# Revit family: Loudspeaker-Bollard-Q-SYS-AD-DWL-Subwoofer
name_source: partatom
category: Communication Devices
units: mm (PartAtom-declared; Revit-internal decimal feet)

## family parameters
Always vertical = Yes
Cut with Voids When Loaded = No
Maintain Annotation Orientation = No
OmniClass Number = 23.85.10.11.14.14.14
OmniClass Title = Loudspeakers
Part Type = Normal
Room Calculation Point = No
Round Connector Dimension = Use Diameter
Shared = No
Work Plane-Based = No

## types (2) — shared parameters
100V Taps = 25 W, 50 W, 100 W
70V Taps = 12.5 W, 25 W, 50 W, 100 W
Body Material = Paint - Q-SYS - Dark Green
Burial Base Diameter = 6.3 "
Burial Base Height = 10.12 "
Conduit Diameter = 0"
Coverage Horizontal = 360.00°
Coverage Vertical = 0.00°
Depth = 6.47 "
Description = Landscape bollard loudspeaker.
Frequency Range = 48 Hz - 200 kHz
Half Width = 3.24 "
Height = 30.17 "
IQ Category = Loudspeaker
Impedance = 16
Length 1 = 1 "
Length 2 = 0.99 "
Length 3 = 3 "
Manufacturer = Q-SYS
Manufacturer URL = www.qsys.com
Model = AD-DWL.SUB
OmniClass Number = 23.85.10.11.14.14.14
Product Documentation Link = https://www.qsys.com
Product Page URL = https://www.qsys.com
Regulatory Compliance = UL1480, CE, ROHS
SPL Max = 112
Sensitivity = 84
URL = www.qsys.com
Weight = 10.36 lbm
Weight Dimensional = 14.8
Weight Product = 10.36
Width = 6.47 "
zero-valued in all types: Cost MSRP, Cost Project, Default Elevation, Heat Load Active, Heat Load Standby, Noise, Offset

## per-type parameters (varying)
| type | Burial Base | Length 4 |
| Dark Green | No | 0 " |
| Dark Green - Burial Base | Yes | 10.12 " |

note: column(s) folded — value = type name in every type: Type Comments

## geometry (parser evidence)
native form markers: Sweep x6
no freeform markers — native parametric forms only
